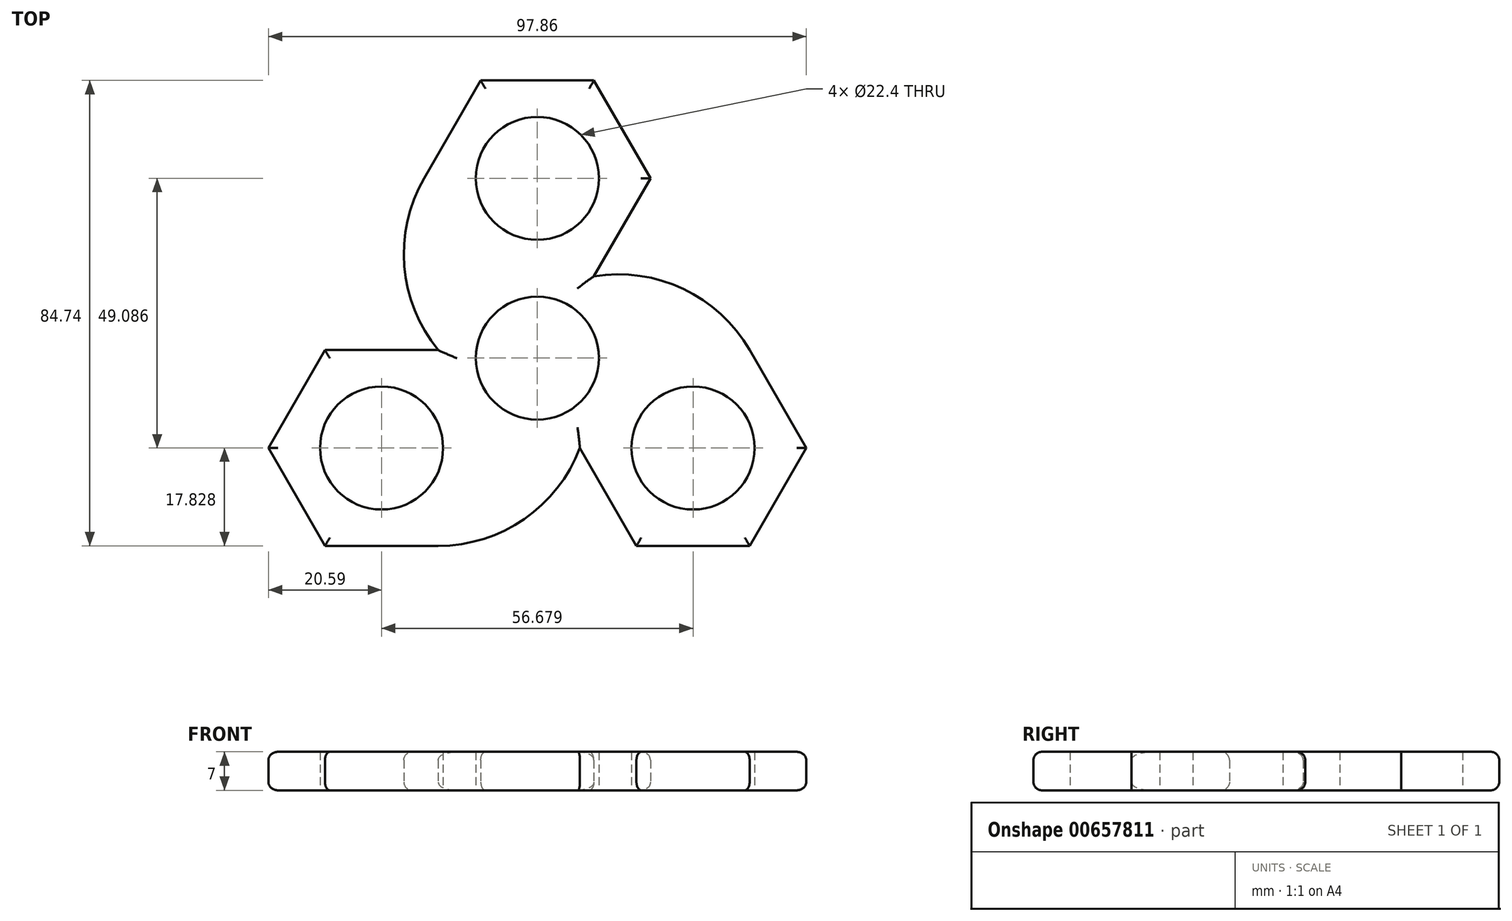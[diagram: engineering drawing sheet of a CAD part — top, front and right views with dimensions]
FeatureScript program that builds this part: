
annotation { "Feature Type Name" : "Feature", "Feature Type Description" : "" }
export const myFeature = defineFeature(function(context is Context, id is Id, definition is map)
    precondition{}
    {
        {
            var Q0;
            Q0=qCreatedBy(makeId("Top.planeOp"),FACE);
            var sketch = newSketch(context, id + "F0", { "sketchPlane" : qUnion([Q0])});
            skCircle(sketch, "E0", {"center": v(0, 0) * mm, "radius": 11.2 * mm});
            skArc(sketch, "E1", {"start": v(11.38, -10.08) * mm, "mid": v(13.16, -7.6) * mm, "end": v(14.42, -4.81) * mm});
            skCircle(sketch, "E2", {"center": v(0, 32.72) * mm, "radius": 11.2 * mm});
            skArc(sketch, "E3.cCircle", {"start": v(7.15, 13.41) * mm, "mid": v(0, 53.31) * mm, "end": v(-7.15, 13.41) * mm, "construction": true});
            skLineSegment(sketch, "E3.0", {"start": v(-20.59, 32.72) * mm, "end": v(-10.3, 50.55) * mm});
            skLineSegment(sketch, "E3.1", {"start": v(-10.3, 50.55) * mm, "end": v(10.3, 50.55) * mm});
            skLineSegment(sketch, "E3.2", {"start": v(10.3, 50.55) * mm, "end": v(20.59, 32.72) * mm});
            skLineSegment(sketch, "E3.3", {"start": v(20.59, 32.72) * mm, "end": v(10.3, 14.9) * mm});
            skLineSegment(sketch, "E3.4", {"start": v(10.3, 14.9) * mm, "end": v(-10.3, 14.9) * mm});
            skLineSegment(sketch, "E3.5", {"start": v(-10.3, 14.9) * mm, "end": v(-20.59, 32.72) * mm});
            skLineSegment(sketch, "E4.1.0", {"start": v(-18.05, -34.2) * mm, "end": v(-38.63, -34.2) * mm});
            skLineSegment(sketch, "E4.1.1", {"start": v(-38.63, -34.2) * mm, "end": v(-48.93, -16.36) * mm});
            skLineSegment(sketch, "E4.1.2", {"start": v(-48.93, -16.36) * mm, "end": v(-38.63, 1.47) * mm});
            skLineSegment(sketch, "E4.1.3", {"start": v(-38.63, 1.47) * mm, "end": v(-18.05, 1.47) * mm});
            skLineSegment(sketch, "E4.1.4", {"start": v(-18.05, 1.47) * mm, "end": v(-7.75, -16.36) * mm});
            skLineSegment(sketch, "E4.1.5", {"start": v(-7.75, -16.36) * mm, "end": v(-18.05, -34.2) * mm});
            skLineSegment(sketch, "E4.2.0", {"start": v(38.63, 1.47) * mm, "end": v(48.93, -16.36) * mm});
            skLineSegment(sketch, "E4.2.1", {"start": v(48.93, -16.36) * mm, "end": v(38.63, -34.2) * mm});
            skLineSegment(sketch, "E4.2.2", {"start": v(38.63, -34.2) * mm, "end": v(18.05, -34.2) * mm});
            skLineSegment(sketch, "E4.2.3", {"start": v(18.05, -34.2) * mm, "end": v(7.75, -16.36) * mm});
            skLineSegment(sketch, "E4.2.4", {"start": v(7.75, -16.36) * mm, "end": v(11.38, -10.08) * mm});
            skLineSegment(sketch, "E4.2.5", {"start": v(18.05, 1.47) * mm, "end": v(38.63, 1.47) * mm});
            skArc(sketch, "E5", {"start": v(-20.59, 32.72) * mm, "mid": v(-24.2, 16.7) * mm, "end": v(-18.05, 1.47) * mm});
            skArc(sketch, "E6.1.0", {"start": v(-18.05, -34.2) * mm, "mid": v(-2.37, -29.3) * mm, "end": v(7.75, -16.36) * mm});
            skArc(sketch, "E6.2.0", {"start": v(38.63, 1.47) * mm, "mid": v(26.56, 12.6) * mm, "end": v(10.3, 14.9) * mm});
            skCircle(sketch, "E7.1.0", {"center": v(-28.34, -16.36) * mm, "radius": 11.2 * mm});
            skCircle(sketch, "E7.2.0", {"center": v(28.34, -16.36) * mm, "radius": 11.2 * mm});
            skArc(sketch, "E8.trimOffspring", {"start": v(7.15, 13.41) * mm, "mid": v(5.15, 14.3) * mm, "end": v(3.04, 14.9) * mm});
            skLineSegment(sketch, "E9.trimOffspring", {"start": v(14.42, -4.81) * mm, "end": v(18.05, 1.47) * mm});
            skArc(sketch, "E10.trimOffspring", {"start": v(-3.04, 14.9) * mm, "mid": v(-5.15, 14.3) * mm, "end": v(-7.15, 13.41) * mm});
            skSolve(sketch);
        }
        {
            var Q0;
            Q0=makeQuery(id+"F0.imprint","IMPRINT",FACE,{"disambiguationData":[TD([[makeQuery(id+"F0.imprint","IMPRINT",EDGE,{"derivedFrom":sQuery(id+"F0.wireOp",EDGE,"E0")}),-1.0]])]});
            var Q1;
            Q1=makeQuery(id+"F0.imprint","IMPRINT",FACE,{"disambiguationData":[TD([[makeQuery(id+"F0.imprint","IMPRINT",EDGE,{"derivedFrom":sQuery(id+"F0.wireOp",EDGE,"E4.1.0")}),-1.0]])]});
            var Q2;
            {var subQ0=sQuery(id+"F0.wireOp",EDGE,"E1");Q2=makeQuery(id+"F0.imprint","IMPRINT",FACE,{"disambiguationData":[TD([[makeQuery(id+"F0.imprint","IMPRINT",EDGE,{"derivedFrom":subQ0}),-1.0]])]});}
            var Q3;
            Q3=makeQuery(id+"F0.imprint","IMPRINT",FACE,{"disambiguationData":[TD([[makeQuery(id+"F0.imprint","IMPRINT",EDGE,{"derivedFrom":sQuery(id+"F0.wireOp",EDGE,"E2")}),-1.0]])]});
            extrude(context, id + "F1", {"entities" : qUnion([Q0, Q1, Q2, Q3]), "depth" : 7 * mm, "offsetDistance" : 25 * mm});
        }
        {
            var Q0;
            Q0=makeQuery(id+"F1.opExtrude","CAP_EDGE",EDGE,{"disambiguationData":[OSD([sQuery(id+"F0.wireOp",EDGE,"E5")])],"isStart":false});
            var Q1;
            Q1=makeQuery(id+"F1.opExtrude","CAP_EDGE",EDGE,{"disambiguationData":[OSD([sQuery(id+"F0.wireOp",EDGE,"E3.0")])],"isStart":false});
            var Q2;
            Q2=makeQuery(id+"F1.opExtrude","CAP_EDGE",EDGE,{"disambiguationData":[OSD([sQuery(id+"F0.wireOp",EDGE,"E3.1")])],"isStart":false});
            var Q3;
            Q3=makeQuery(id+"F1.opExtrude","CAP_EDGE",EDGE,{"disambiguationData":[OSD([sQuery(id+"F0.wireOp",EDGE,"E3.2")])],"isStart":false});
            var Q4;
            Q4=makeQuery(id+"F1.opExtrude","CAP_EDGE",EDGE,{"disambiguationData":[OSD([sQuery(id+"F0.wireOp",EDGE,"E3.3")])],"isStart":false});
            var Q5;
            Q5=makeQuery(id+"F1.opExtrude","CAP_EDGE",EDGE,{"disambiguationData":[OSD([sQuery(id+"F0.wireOp",EDGE,"E6.2.0")])],"isStart":false});
            var Q6;
            Q6=makeQuery(id+"F1.opExtrude","CAP_EDGE",EDGE,{"disambiguationData":[OSD([sQuery(id+"F0.wireOp",EDGE,"E4.2.0")])],"isStart":false});
            var Q7;
            Q7=makeQuery(id+"F1.opExtrude","CAP_EDGE",EDGE,{"disambiguationData":[OSD([sQuery(id+"F0.wireOp",EDGE,"E4.2.1")])],"isStart":false});
            var Q8;
            Q8=makeQuery(id+"F1.opExtrude","CAP_EDGE",EDGE,{"disambiguationData":[OSD([sQuery(id+"F0.wireOp",EDGE,"E4.2.2")])],"isStart":false});
            var Q9;
            Q9=makeQuery(id+"F1.opExtrude","CAP_EDGE",EDGE,{"disambiguationData":[OSD([sQuery(id+"F0.wireOp",EDGE,"E4.2.3")])],"isStart":false});
            var Q10;
            Q10=makeQuery(id+"F1.opExtrude","CAP_EDGE",EDGE,{"disambiguationData":[OSD([sQuery(id+"F0.wireOp",EDGE,"E6.1.0")])],"isStart":false});
            var Q11;
            Q11=makeQuery(id+"F1.opExtrude","CAP_EDGE",EDGE,{"disambiguationData":[OSD([sQuery(id+"F0.wireOp",EDGE,"E4.1.0")])],"isStart":false});
            var Q12;
            Q12=makeQuery(id+"F1.opExtrude","CAP_EDGE",EDGE,{"disambiguationData":[OSD([sQuery(id+"F0.wireOp",EDGE,"E4.1.1")])],"isStart":false});
            var Q13;
            Q13=makeQuery(id+"F1.opExtrude","CAP_EDGE",EDGE,{"disambiguationData":[OSD([sQuery(id+"F0.wireOp",EDGE,"E4.1.2")])],"isStart":false});
            var Q14;
            Q14=makeQuery(id+"F1.opExtrude","CAP_EDGE",EDGE,{"disambiguationData":[OSD([sQuery(id+"F0.wireOp",EDGE,"E4.1.3")])],"isStart":false});
            fillet(context, id + "F2", {"entities" : qUnion([Q0, Q1, Q2, Q3, Q4, Q5, Q6, Q7, Q8, Q9, Q10, Q11, Q12, Q13, Q14]), "radius" : 1.5 * mm, "tangentPropagation" : true, "allowEdgeOverflow" : false});
        }
        {
            var Q0;
            Q0=makeQuery(id+"F1.opExtrude","CAP_EDGE",EDGE,{"disambiguationData":[OSD([sQuery(id+"F0.wireOp",EDGE,"E4.1.0")])],"isStart":true});
            var Q1;
            Q1=makeQuery(id+"F1.opExtrude","CAP_EDGE",EDGE,{"disambiguationData":[OSD([sQuery(id+"F0.wireOp",EDGE,"E6.1.0")])],"isStart":true});
            var Q2;
            Q2=makeQuery(id+"F1.opExtrude","CAP_EDGE",EDGE,{"disambiguationData":[OSD([sQuery(id+"F0.wireOp",EDGE,"E4.2.3")])],"isStart":true});
            var Q3;
            Q3=makeQuery(id+"F1.opExtrude","CAP_EDGE",EDGE,{"disambiguationData":[OSD([sQuery(id+"F0.wireOp",EDGE,"E4.2.2")])],"isStart":true});
            var Q4;
            Q4=makeQuery(id+"F1.opExtrude","CAP_EDGE",EDGE,{"disambiguationData":[OSD([sQuery(id+"F0.wireOp",EDGE,"E4.2.1")])],"isStart":true});
            var Q5;
            Q5=makeQuery(id+"F1.opExtrude","CAP_EDGE",EDGE,{"disambiguationData":[OSD([sQuery(id+"F0.wireOp",EDGE,"E4.2.0")])],"isStart":true});
            var Q6;
            Q6=makeQuery(id+"F1.opExtrude","CAP_EDGE",EDGE,{"disambiguationData":[OSD([sQuery(id+"F0.wireOp",EDGE,"E6.2.0")])],"isStart":true});
            var Q7;
            Q7=makeQuery(id+"F1.opExtrude","CAP_EDGE",EDGE,{"disambiguationData":[OSD([sQuery(id+"F0.wireOp",EDGE,"E3.3")])],"isStart":true});
            var Q8;
            Q8=makeQuery(id+"F1.opExtrude","CAP_EDGE",EDGE,{"disambiguationData":[OSD([sQuery(id+"F0.wireOp",EDGE,"E3.2")])],"isStart":true});
            var Q9;
            Q9=makeQuery(id+"F1.opExtrude","CAP_EDGE",EDGE,{"disambiguationData":[OSD([sQuery(id+"F0.wireOp",EDGE,"E3.1")])],"isStart":true});
            var Q10;
            Q10=makeQuery(id+"F1.opExtrude","CAP_EDGE",EDGE,{"disambiguationData":[OSD([sQuery(id+"F0.wireOp",EDGE,"E3.0")])],"isStart":true});
            var Q11;
            Q11=makeQuery(id+"F1.opExtrude","CAP_EDGE",EDGE,{"disambiguationData":[OSD([sQuery(id+"F0.wireOp",EDGE,"E5")])],"isStart":true});
            var Q12;
            Q12=makeQuery(id+"F1.opExtrude","CAP_EDGE",EDGE,{"disambiguationData":[OSD([sQuery(id+"F0.wireOp",EDGE,"E4.1.3")])],"isStart":true});
            var Q13;
            Q13=makeQuery(id+"F1.opExtrude","CAP_EDGE",EDGE,{"disambiguationData":[OSD([sQuery(id+"F0.wireOp",EDGE,"E4.1.2")])],"isStart":true});
            var Q14;
            Q14=makeQuery(id+"F1.opExtrude","CAP_EDGE",EDGE,{"disambiguationData":[OSD([sQuery(id+"F0.wireOp",EDGE,"E4.1.1")])],"isStart":true});
            fillet(context, id + "F3", {"entities" : qUnion([Q0, Q1, Q2, Q3, Q4, Q5, Q6, Q7, Q8, Q9, Q10, Q11, Q12, Q13, Q14]), "radius" : 1.5 * mm, "tangentPropagation" : true, "allowEdgeOverflow" : false});
        }
    });
